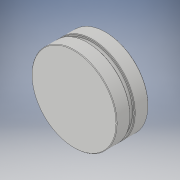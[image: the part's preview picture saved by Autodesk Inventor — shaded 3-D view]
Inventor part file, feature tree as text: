
AUTODESK INVENTOR PART (.ipt)
format: ipt  version: 2018 (Build 220112000, 112)  size: 139,776 bytes
history: native  units: in
note: dims shown in document units (in); Inventor stores cm internally (conversion verified against a paired STEP export)
features: extrude x2, sketch x2, plane x1, fillet x1
ambient origin geometry x8: Origin, YZ Plane, XZ Plane, XY Plane, X Axis, Y Axis, Z Axis, Center Point
bodies: Solid1 (feature_tree)
feature tree (6):
  extrude  "Extrusion1"  Depth=0.5906in TaperAngle=0.0deg
  plane  "Work Plane1"
  extrude  "Extrusion2"  Depth=0.0098in
  fillet  "Fillet1"  Radius=0.0787in
  sketch  "Sketch1"  dims[d0=1.5748in d1=0.5906in d2=0.0in]
  sketch  "Sketch2"  dims[d3=-0.3346in d4=1.4961in d5=0.0787in d6=0.0in d7=0.0098in]
